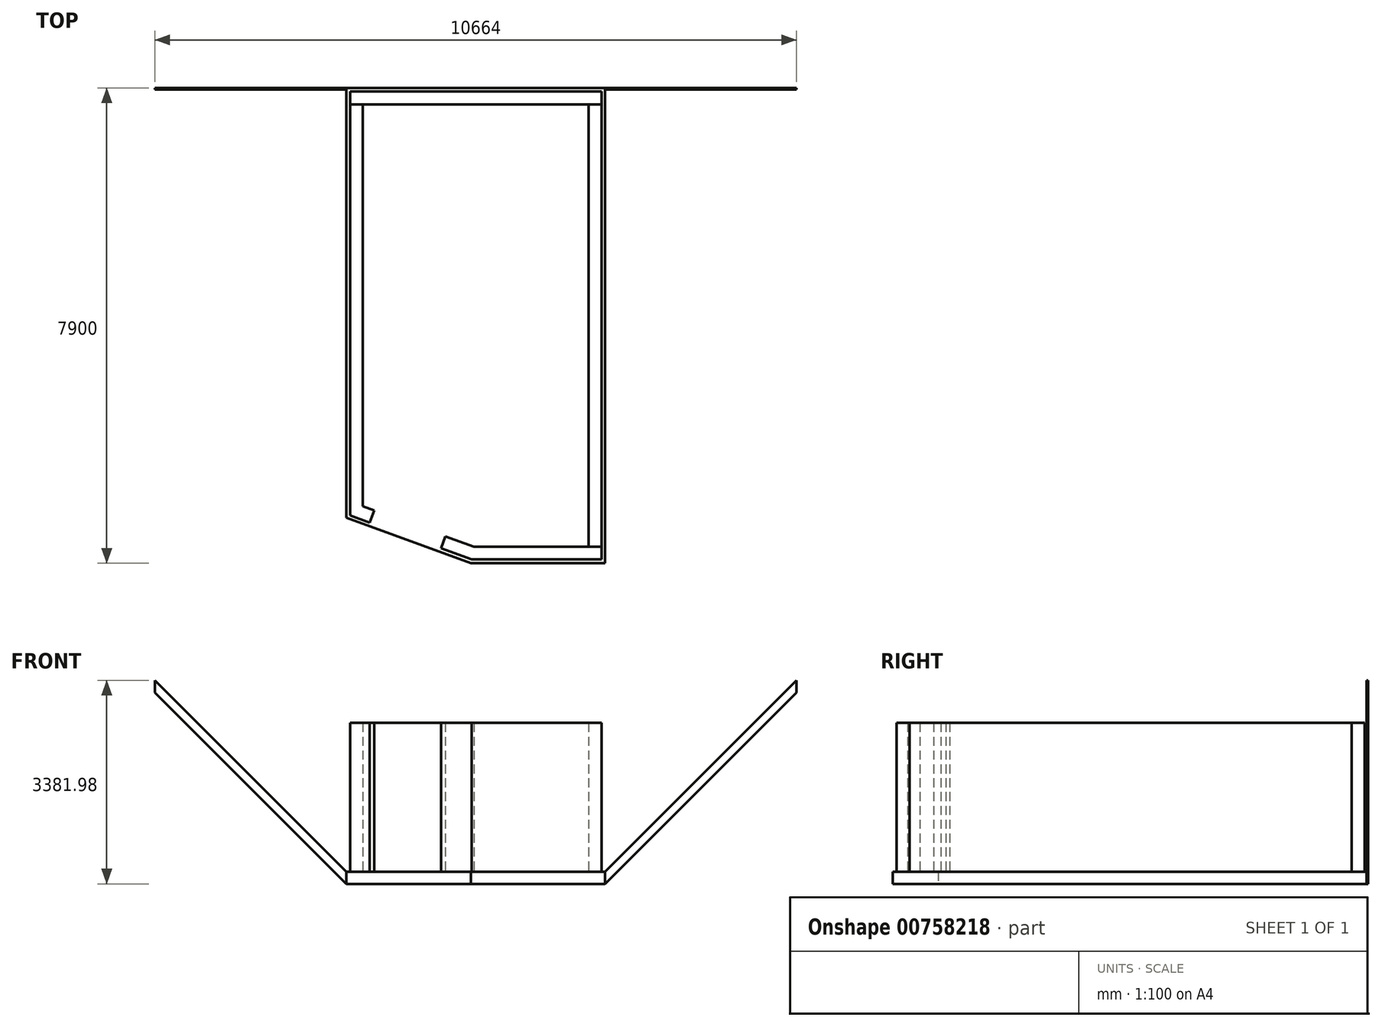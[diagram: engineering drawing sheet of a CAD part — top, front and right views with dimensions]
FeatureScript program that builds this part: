
annotation { "Feature Type Name" : "Feature", "Feature Type Description" : "" }
export const myFeature = defineFeature(function(context is Context, id is Id, definition is map)
    precondition{}
    {
        {
            var Q0;
            Q0=qCreatedBy(makeId("Top.planeOp"),FACE);
            var sketch = newSketch(context, id + "F0", { "sketchPlane" : qUnion([Q0])});
            skLineSegment(sketch, "E0.bottom", {"start": v(1686.13, 342.48) * mm, "end": v(3915.99, 342.48) * mm});
            skLineSegment(sketch, "E0.top", {"start": v(-384.01, 8242.48) * mm, "end": v(3915.99, 8242.48) * mm});
            skLineSegment(sketch, "E0.left", {"start": v(-384.01, 1095.95) * mm, "end": v(-384.01, 8242.48) * mm});
            skLineSegment(sketch, "E0.right", {"start": v(3915.99, 342.48) * mm, "end": v(3915.99, 8242.48) * mm});
            skLineSegment(sketch, "E1", {"start": v(-384.01, 1095.95) * mm, "end": v(1686.13, 342.48) * mm});
            skSolve(sketch);
        }
        {
            var Q0;
            Q0=makeQuery(id+"F0.imprint","IMPRINT",FACE,{"disambiguationData":[TD([[makeQuery(id+"F0.imprint","IMPRINT",EDGE,{"derivedFrom":sQuery(id+"F0.wireOp",EDGE,"E0.bottom")}),1.0]])]});
            extrude(context, id + "F1", {"entities" : qUnion([Q0]), "depth" : 200 * mm, "offsetDistance" : 25 * mm});
        }
        {
            var Q0;
            Q0=makeQuery(id+"F1.opExtrude","CAP_FACE",FACE,{"disambiguationData":[OSD([sQuery(id+"F0.wireOp",EDGE,"E0.bottom"),sQuery(id+"F0.wireOp",EDGE,"E0.top"),sQuery(id+"F0.wireOp",EDGE,"E0.left"),sQuery(id+"F0.wireOp",EDGE,"E0.right")])],"isStart":false});
            var sketch = newSketch(context, id + "F2", { "sketchPlane" : qUnion([Q0])});
            skLineSegment(sketch, "E2.bottom", {"start": v(3855.99, 617.48) * mm, "end": v(3640.99, 617.48) * mm});
            skLineSegment(sketch, "E2.top", {"start": v(3855.99, 7967.48) * mm, "end": v(3640.99, 7967.48) * mm});
            skLineSegment(sketch, "E2.left", {"start": v(3855.99, 617.48) * mm, "end": v(3855.99, 7967.48) * mm});
            skLineSegment(sketch, "E2.right", {"start": v(3640.99, 617.48) * mm, "end": v(3640.99, 7967.48) * mm});
            skSolve(sketch);
        }
        {
            var Q0;
            Q0=makeQuery(id+"F2.imprint","IMPRINT",FACE,{"disambiguationData":[TD([[makeQuery(id+"F2.imprint","IMPRINT",EDGE,{"derivedFrom":sQuery(id+"F2.wireOp",EDGE,"E2.bottom")}),-1.0]])]});
            extrude(context, id + "F3", {"entities" : qUnion([Q0]), "depth" : 2475 * mm, "offsetDistance" : 25 * mm});
        }
        {
            var Q0;
            Q0=makeQuery(id+"F1.opExtrude","CAP_FACE",FACE,{"disambiguationData":[OSD([sQuery(id+"F0.wireOp",EDGE,"E0.bottom"),sQuery(id+"F0.wireOp",EDGE,"E0.top"),sQuery(id+"F0.wireOp",EDGE,"E0.left"),sQuery(id+"F0.wireOp",EDGE,"E0.right"),sQuery(id+"F0.wireOp",EDGE,"E1")])],"isStart":false});
            var sketch = newSketch(context, id + "F4", { "sketchPlane" : qUnion([Q0])});
            skLineSegment(sketch, "E3", {"start": v(-324.01, 7967.48) * mm, "end": v(-324.01, 1137.96) * mm});
            skLineSegment(sketch, "E4", {"start": v(-324.01, 1137.96) * mm, "end": v(5.4, 1018.07) * mm});
            skLineSegment(sketch, "E5", {"start": v(5.4, 1018.07) * mm, "end": v(78.93, 1220.1) * mm});
            skLineSegment(sketch, "E6", {"start": v(78.93, 1220.1) * mm, "end": v(-109.01, 1288.5) * mm});
            skLineSegment(sketch, "E7", {"start": v(-109.01, 1288.5) * mm, "end": v(-109.01, 7967.48) * mm});
            skLineSegment(sketch, "E8", {"start": v(-109.01, 7967.48) * mm, "end": v(-324.01, 7967.48) * mm});
            skSolve(sketch);
        }
        {
            var Q0;
            Q0=makeQuery(id+"F4.imprint","IMPRINT",FACE,{"disambiguationData":[TD([[makeQuery(id+"F4.imprint","IMPRINT",EDGE,{"derivedFrom":sQuery(id+"F4.wireOp",EDGE,"E3")}),1.0]])]});
            extrude(context, id + "F5", {"entities" : qUnion([Q0]), "depth" : 2475 * mm, "offsetDistance" : 25 * mm});
        }
        {
            var Q0;
            Q0=makeQuery(id+"F1.opExtrude","CAP_FACE",FACE,{"disambiguationData":[OSD([sQuery(id+"F0.wireOp",EDGE,"E0.bottom"),sQuery(id+"F0.wireOp",EDGE,"E0.top"),sQuery(id+"F0.wireOp",EDGE,"E0.left"),sQuery(id+"F0.wireOp",EDGE,"E0.right")])],"isStart":false});
            var sketch = newSketch(context, id + "F6", { "sketchPlane" : qUnion([Q0])});
            skLineSegment(sketch, "E9.bottom", {"start": v(3855.99, 7967.48) * mm, "end": v(-324.01, 7967.48) * mm});
            skLineSegment(sketch, "E9.top", {"start": v(3855.99, 8182.48) * mm, "end": v(-324.01, 8182.48) * mm});
            skLineSegment(sketch, "E9.left", {"start": v(3855.99, 7967.48) * mm, "end": v(3855.99, 8182.48) * mm});
            skLineSegment(sketch, "E9.right", {"start": v(-324.01, 7967.48) * mm, "end": v(-324.01, 8182.48) * mm});
            skSolve(sketch);
        }
        {
            var Q0;
            Q0=makeQuery(id+"F6.imprint","IMPRINT",FACE,{"disambiguationData":[TD([[makeQuery(id+"F6.imprint","IMPRINT",EDGE,{"derivedFrom":sQuery(id+"F6.wireOp",EDGE,"E9.bottom")}),-1.0]])]});
            extrude(context, id + "F7", {"entities" : qUnion([Q0]), "depth" : 2475 * mm, "offsetDistance" : 25 * mm});
        }
        {
            var Q0;
            Q0=makeQuery(id+"F1.opExtrude","SWEPT_FACE",FACE,{"disambiguationData":[OSD([sQuery(id+"F0.wireOp",EDGE,"E0.top")])]});
            var sketch = newSketch(context, id + "F8", { "sketchPlane" : qUnion([Q0])});
            skPoint(sketch, "E10.0", {"position": v(-3915.99, 200) * mm});
            skPoint(sketch, "E11.0", {"position": v(-3915.99, 0) * mm});
            skPoint(sketch, "E12.0", {"position": v(384.01, 200) * mm});
            skPoint(sketch, "E13.0", {"position": v(384.01, 0) * mm});
            skLineSegment(sketch, "E14", {"start": v(-3915.99, 0) * mm, "end": v(-3915.99, 200) * mm});
            skLineSegment(sketch, "E15", {"start": v(-3915.99, 200) * mm, "end": v(-7097.97, 3381.98) * mm});
            skLineSegment(sketch, "E16", {"start": v(-3915.99, 0) * mm, "end": v(-7097.97, 3181.98) * mm});
            skLineSegment(sketch, "E17", {"start": v(-7097.97, 3181.98) * mm, "end": v(-7097.97, 3381.98) * mm});
            skLineSegment(sketch, "E18", {"start": v(384.01, 0) * mm, "end": v(384.01, 200) * mm});
            skLineSegment(sketch, "E19", {"start": v(384.01, 200) * mm, "end": v(3566, 3381.98) * mm});
            skLineSegment(sketch, "E20", {"start": v(384.01, 0) * mm, "end": v(3566, 3181.98) * mm});
            skLineSegment(sketch, "E21", {"start": v(3566, 3181.98) * mm, "end": v(3566, 3381.98) * mm});
            skSolve(sketch);
        }
        {
            var Q0;
            Q0=makeQuery(id+"F8.imprint","IMPRINT",FACE,{"disambiguationData":[TD([[makeQuery(id+"F8.imprint","IMPRINT",EDGE,{"derivedFrom":sQuery(id+"F8.wireOp",EDGE,"E14")}),-1.0]])]});
            extrude(context, id + "F9", {"entities" : qUnion([Q0]), "oppositeDirection" : true, "depth" : 25 * mm, "offsetDistance" : 25 * mm});
        }
        {
            var Q0;
            Q0=makeQuery(id+"F8.imprint","IMPRINT",FACE,{"disambiguationData":[TD([[makeQuery(id+"F8.imprint","IMPRINT",EDGE,{"derivedFrom":sQuery(id+"F8.wireOp",EDGE,"E18")}),1.0]])]});
            extrude(context, id + "F10", {"entities" : qUnion([Q0]), "oppositeDirection" : true, "depth" : 25 * mm, "offsetDistance" : 25 * mm});
        }
        {
            var Q0;
            Q0=makeQuery(id+"F1.opExtrude","CAP_FACE",FACE,{"disambiguationData":[OSD([sQuery(id+"F0.wireOp",EDGE,"E0.bottom"),sQuery(id+"F0.wireOp",EDGE,"E0.top"),sQuery(id+"F0.wireOp",EDGE,"E0.left"),sQuery(id+"F0.wireOp",EDGE,"E0.right"),sQuery(id+"F0.wireOp",EDGE,"E1")])],"isStart":false});
            var sketch = newSketch(context, id + "F11", { "sketchPlane" : qUnion([Q0])});
            skLineSegment(sketch, "E22.bottom", {"start": v(3855.99, 617.48) * mm, "end": v(1734.62, 617.48) * mm});
            skLineSegment(sketch, "E22.top", {"start": v(3855.99, 402.48) * mm, "end": v(1696.71, 402.48) * mm});
            skLineSegment(sketch, "E22.left", {"start": v(3855.99, 617.48) * mm, "end": v(3855.99, 402.48) * mm});
            skLineSegment(sketch, "E23", {"start": v(1696.71, 402.48) * mm, "end": v(1189.4, 587.12) * mm});
            skLineSegment(sketch, "E24", {"start": v(1189.4, 587.12) * mm, "end": v(1262.94, 789.16) * mm});
            skLineSegment(sketch, "E25", {"start": v(1262.94, 789.16) * mm, "end": v(1734.62, 617.48) * mm});
            skSolve(sketch);
        }
        {
            var Q0;
            Q0=makeQuery(id+"F11.imprint","IMPRINT",FACE,{"disambiguationData":[TD([[makeQuery(id+"F11.imprint","IMPRINT",EDGE,{"derivedFrom":sQuery(id+"F11.wireOp",EDGE,"E22.bottom")}),1.0]])]});
            extrude(context, id + "F12", {"entities" : qUnion([Q0]), "depth" : 2475 * mm, "offsetDistance" : 25 * mm});
        }
    });
